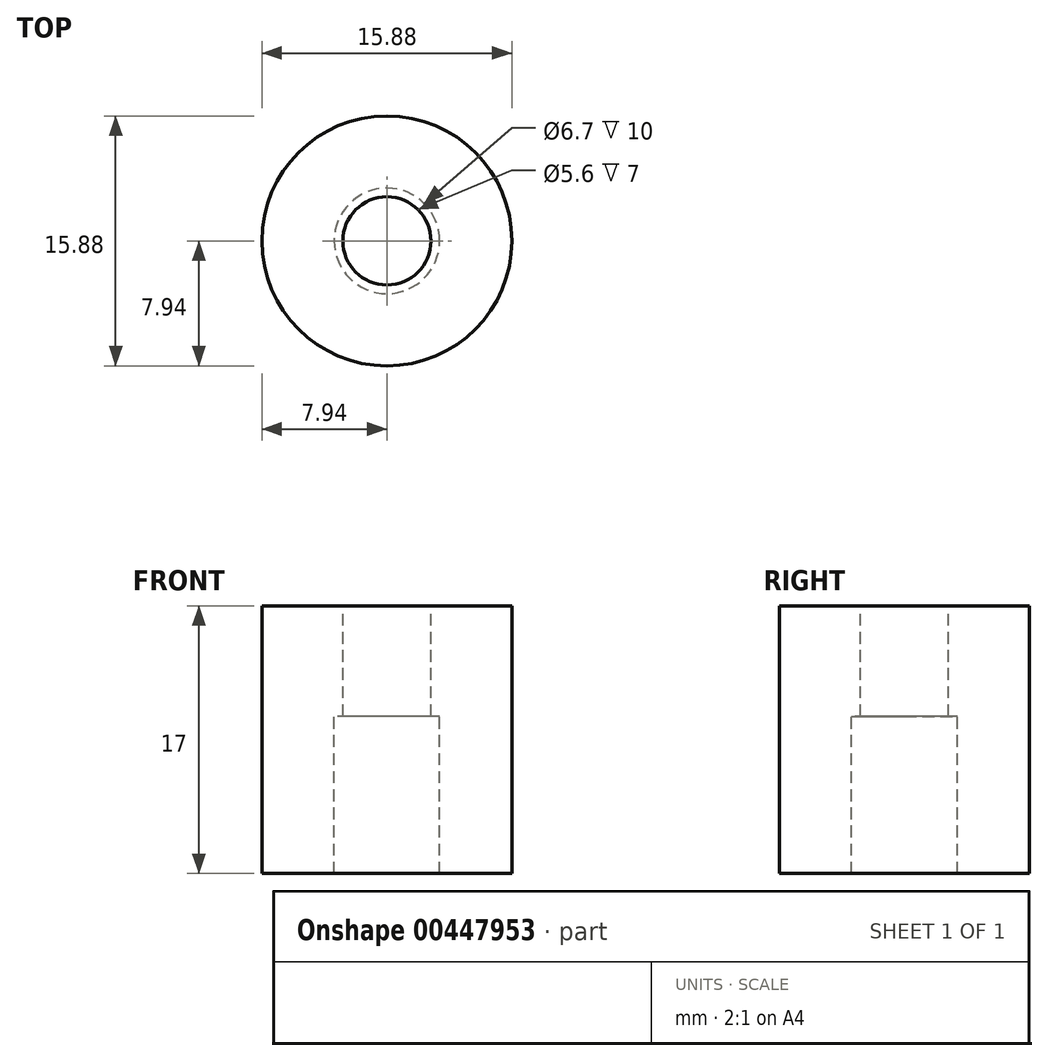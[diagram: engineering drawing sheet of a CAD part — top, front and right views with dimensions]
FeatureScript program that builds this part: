
annotation { "Feature Type Name" : "Feature", "Feature Type Description" : "" }
export const myFeature = defineFeature(function(context is Context, id is Id, definition is map)
    precondition{}
    {
        {
            var Q0;
            Q0=qCreatedBy(makeId("Front.planeOp"),FACE);
            var sketch = newSketch(context, id + "F0", { "sketchPlane" : qUnion([Q0])});
            skLineSegment(sketch, "E0", {"start": v(-7.94, 7) * mm, "end": v(-7.94, -10) * mm});
            skLineSegment(sketch, "E1", {"start": v(-7.94, -10) * mm, "end": v(-3.35, -10) * mm});
            skLineSegment(sketch, "E2", {"start": v(-3.35, -10) * mm, "end": v(-3.35, 0) * mm});
            skLineSegment(sketch, "E3", {"start": v(-3.35, 0) * mm, "end": v(-2.8, 0) * mm});
            skLineSegment(sketch, "E4", {"start": v(-2.8, 0) * mm, "end": v(-2.8, 7) * mm});
            skLineSegment(sketch, "E5", {"start": v(-2.8, 7) * mm, "end": v(-7.94, 7) * mm});
            skLineSegment(sketch, "E6", {"start": v(0, 7) * mm, "end": v(0, -10) * mm, "construction": true});
            skSolve(sketch);
        }
        {
            var Q0;
            Q0=makeQuery(id+"F0.imprint","IMPRINT",FACE,{"disambiguationData":[TD([[makeQuery(id+"F0.imprint","IMPRINT",EDGE,{"derivedFrom":sQuery(id+"F0.wireOp",EDGE,"E0")}),1.0]])]});
            var Q1;
            Q1=sQuery(id+"F0.wireOp",EDGE,"E6");
            revolve(context, id + "F1", {"entities" : qUnion([Q0]), "axis" : qUnion([Q1]), "revolveType" : RevolveType.FULL});
        }
    });
